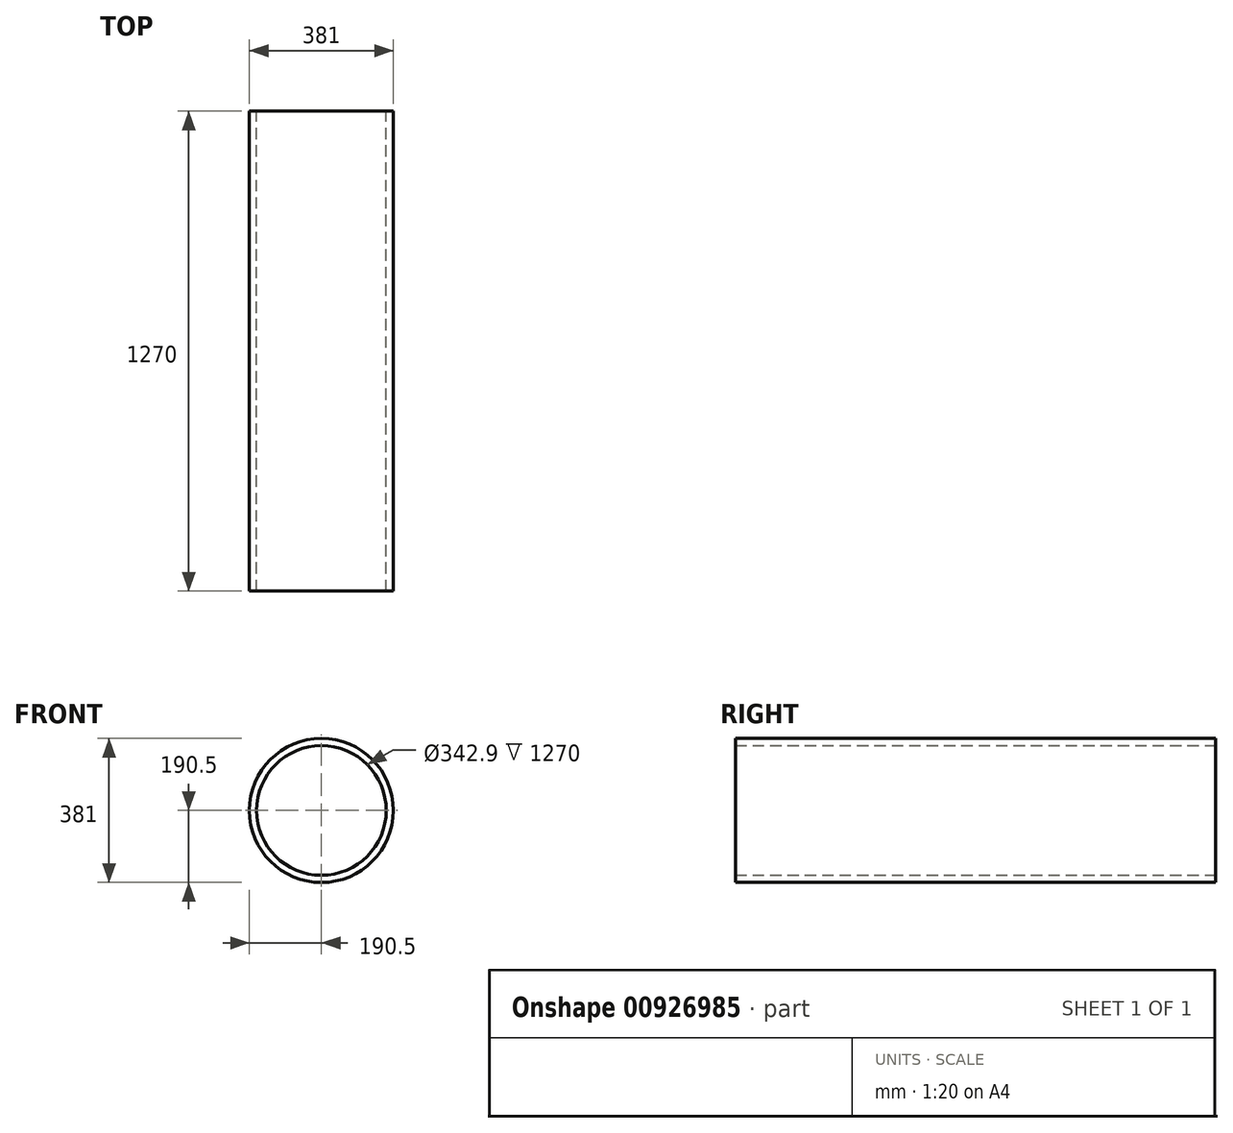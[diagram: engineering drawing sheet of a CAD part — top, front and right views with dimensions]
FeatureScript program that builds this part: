
annotation { "Feature Type Name" : "Feature", "Feature Type Description" : "" }
export const myFeature = defineFeature(function(context is Context, id is Id, definition is map)
    precondition{}
    {
        {
            var Q0;
            Q0=qCreatedBy(makeId("Front.planeOp"),FACE);
            var sketch = newSketch(context, id + "F0", { "sketchPlane" : qUnion([Q0])});
            skCircle(sketch, "E0", {"center": v(0, 0) * mm, "radius": 190.5 * mm});
            skCircle(sketch, "E1", {"center": v(0, 0) * mm, "radius": 171.45 * mm});
            skSolve(sketch);
        }
        {
            var Q0;
            Q0=makeQuery(id+"F0.imprint","IMPRINT",FACE,{"disambiguationData":[TD([[makeQuery(id+"F0.imprint","IMPRINT",EDGE,{"derivedFrom":sQuery(id+"F0.wireOp",EDGE,"E0")}),1.0]])]});
            extrude(context, id + "F1", {"entities" : qUnion([Q0]), "depth" : 1270 * mm, "offsetDistance" : 25.4 * mm});
        }
    });
